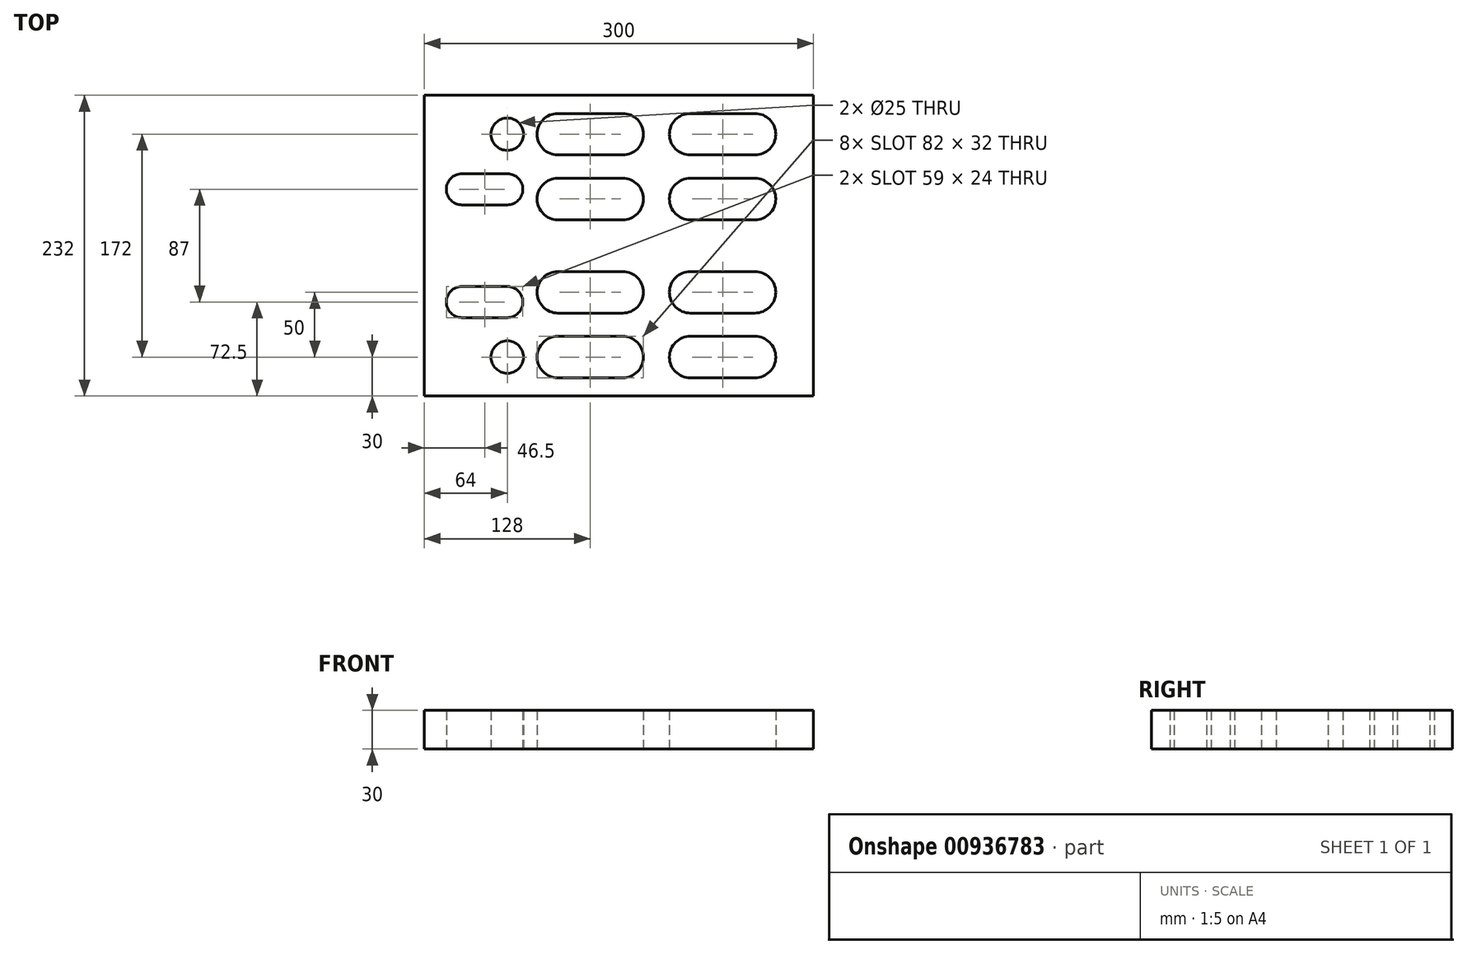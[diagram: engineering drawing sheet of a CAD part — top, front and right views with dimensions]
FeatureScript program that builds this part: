
annotation { "Feature Type Name" : "Feature", "Feature Type Description" : "" }
export const myFeature = defineFeature(function(context is Context, id is Id, definition is map)
    precondition{}
    {
        {
            var Q0;
            Q0=qCreatedBy(makeId("Top.planeOp"),FACE);
            var sketch = newSketch(context, id + "F0", { "sketchPlane" : qUnion([Q0])});
            skLineSegment(sketch, "E0.bottom", {"start": v(300, 116) * mm, "end": v(0, 116) * mm});
            skLineSegment(sketch, "E0.top", {"start": v(300, -116) * mm, "end": v(0, -116) * mm});
            skLineSegment(sketch, "E0.left", {"start": v(300, 116) * mm, "end": v(300, -116) * mm});
            skLineSegment(sketch, "E0.right", {"start": v(0, 116) * mm, "end": v(0, -116) * mm});
            skPoint(sketch, "E0.middle", {"position": v(0, 0) * mm});
            skArc(sketch, "E1", {"start": v(103, 102) * mm, "mid": v(87, 86) * mm, "end": v(103, 70) * mm});
            skArc(sketch, "E2", {"start": v(153, 70) * mm, "mid": v(169, 86) * mm, "end": v(153, 102) * mm});
            skLineSegment(sketch, "E3", {"start": v(103, 102) * mm, "end": v(153, 102) * mm});
            skLineSegment(sketch, "E4", {"start": v(103, 70) * mm, "end": v(153, 70) * mm});
            skLineSegment(sketch, "E5.1.0.0", {"start": v(205, 102) * mm, "end": v(255, 102) * mm});
            skArc(sketch, "E5.1.0.1", {"start": v(205, 102) * mm, "mid": v(189, 86) * mm, "end": v(205, 70) * mm});
            skLineSegment(sketch, "E5.1.0.2", {"start": v(205, 70) * mm, "end": v(255, 70) * mm});
            skArc(sketch, "E5.1.0.3", {"start": v(255, 70) * mm, "mid": v(271, 86) * mm, "end": v(255, 102) * mm});
            skLineSegment(sketch, "E5.direction1", {"start": v(103, 102) * mm, "end": v(205, 102) * mm, "construction": true});
            skArc(sketch, "E6.0.1.0", {"start": v(103, 52) * mm, "mid": v(87, 36) * mm, "end": v(103, 20) * mm});
            skLineSegment(sketch, "E6.0.1.1", {"start": v(103, 52) * mm, "end": v(153, 52) * mm});
            skArc(sketch, "E6.0.1.2", {"start": v(153, 20) * mm, "mid": v(169, 36) * mm, "end": v(153, 52) * mm});
            skLineSegment(sketch, "E6.0.1.3", {"start": v(103, 20) * mm, "end": v(153, 20) * mm});
            skArc(sketch, "E6.0.1.4", {"start": v(205, 52) * mm, "mid": v(189, 36) * mm, "end": v(205, 20) * mm});
            skLineSegment(sketch, "E6.0.1.5", {"start": v(205, 52) * mm, "end": v(255, 52) * mm});
            skArc(sketch, "E6.0.1.6", {"start": v(255, 20) * mm, "mid": v(271, 36) * mm, "end": v(255, 52) * mm});
            skLineSegment(sketch, "E6.0.1.7", {"start": v(205, 20) * mm, "end": v(255, 20) * mm});
            skLineSegment(sketch, "E6.direction1", {"start": v(103, 70) * mm, "end": v(128, 70) * mm, "construction": true});
            skLineSegment(sketch, "E6.direction2", {"start": v(103, 70) * mm, "end": v(103, 20) * mm, "construction": true});
            skCircle(sketch, "E7", {"center": v(64, 86) * mm, "radius": 12.5 * mm});
            skArc(sketch, "E8", {"start": v(29, 55.5) * mm, "mid": v(17, 43.5) * mm, "end": v(29, 31.5) * mm});
            skArc(sketch, "E9", {"start": v(64, 31.5) * mm, "mid": v(76, 43.5) * mm, "end": v(64, 55.5) * mm});
            skLineSegment(sketch, "E10", {"start": v(29, 55.5) * mm, "end": v(64, 55.5) * mm});
            skLineSegment(sketch, "E11", {"start": v(64, 31.5) * mm, "end": v(29, 31.5) * mm});
            skCircle(sketch, "E12.MirrorC", {"center": v(64, -86) * mm, "radius": 12.5 * mm});
            skLineSegment(sketch, "E13.MirrorCS", {"start": v(29, -55.5) * mm, "end": v(64, -55.5) * mm});
            skArc(sketch, "E14.MirrorCS", {"start": v(29, -55.5) * mm, "mid": v(17, -43.5) * mm, "end": v(29, -31.5) * mm});
            skLineSegment(sketch, "E15.MirrorCS", {"start": v(64, -31.5) * mm, "end": v(29, -31.5) * mm});
            skArc(sketch, "E16.MirrorCS", {"start": v(64, -31.5) * mm, "mid": v(76, -43.5) * mm, "end": v(64, -55.5) * mm});
            skArc(sketch, "E17.MirrorCS", {"start": v(103, -102) * mm, "mid": v(87, -86) * mm, "end": v(103, -70) * mm});
            skLineSegment(sketch, "E18.MirrorCS", {"start": v(103, -70) * mm, "end": v(153, -70) * mm});
            skArc(sketch, "E19.MirrorCS", {"start": v(153, -70) * mm, "mid": v(169, -86) * mm, "end": v(153, -102) * mm});
            skLineSegment(sketch, "E20.MirrorCS", {"start": v(103, -102) * mm, "end": v(153, -102) * mm});
            skLineSegment(sketch, "E21.MirrorCS", {"start": v(103, -52) * mm, "end": v(153, -52) * mm});
            skArc(sketch, "E22.MirrorCS", {"start": v(103, -52) * mm, "mid": v(87, -36) * mm, "end": v(103, -20) * mm});
            skLineSegment(sketch, "E23.MirrorCS", {"start": v(103, -20) * mm, "end": v(153, -20) * mm});
            skArc(sketch, "E24.MirrorCS", {"start": v(153, -20) * mm, "mid": v(169, -36) * mm, "end": v(153, -52) * mm});
            skArc(sketch, "E25.MirrorCS", {"start": v(205, -52) * mm, "mid": v(189, -36) * mm, "end": v(205, -20) * mm});
            skLineSegment(sketch, "E26.MirrorCS", {"start": v(205, -52) * mm, "end": v(255, -52) * mm});
            skArc(sketch, "E27.MirrorCS", {"start": v(255, -20) * mm, "mid": v(271, -36) * mm, "end": v(255, -52) * mm});
            skLineSegment(sketch, "E28.MirrorCS", {"start": v(205, -20) * mm, "end": v(255, -20) * mm});
            skArc(sketch, "E29.MirrorCS", {"start": v(205, -102) * mm, "mid": v(189, -86) * mm, "end": v(205, -70) * mm});
            skLineSegment(sketch, "E30.MirrorCS", {"start": v(205, -102) * mm, "end": v(255, -102) * mm});
            skArc(sketch, "E31.MirrorCS", {"start": v(255, -70) * mm, "mid": v(271, -86) * mm, "end": v(255, -102) * mm});
            skLineSegment(sketch, "E32.MirrorCS", {"start": v(205, -70) * mm, "end": v(255, -70) * mm});
            skArc(sketch, "E33.0", {"start": v(103, 101) * mm, "mid": v(88, 86) * mm, "end": v(103, 71) * mm});
            skLineSegment(sketch, "E33.1", {"start": v(103, 101) * mm, "end": v(153, 101) * mm});
            skArc(sketch, "E33.2", {"start": v(153, 71) * mm, "mid": v(168, 86) * mm, "end": v(153, 101) * mm});
            skLineSegment(sketch, "E33.3", {"start": v(103, 71) * mm, "end": v(153, 71) * mm});
            skArc(sketch, "E34.0", {"start": v(205, 101) * mm, "mid": v(190, 86) * mm, "end": v(205, 71) * mm});
            skLineSegment(sketch, "E34.1", {"start": v(205, 101) * mm, "end": v(255, 101) * mm});
            skArc(sketch, "E34.2", {"start": v(255, 71) * mm, "mid": v(270, 86) * mm, "end": v(255, 101) * mm});
            skLineSegment(sketch, "E34.3", {"start": v(205, 71) * mm, "end": v(255, 71) * mm});
            skArc(sketch, "E35.0", {"start": v(205, 51) * mm, "mid": v(190, 36) * mm, "end": v(205, 21) * mm});
            skLineSegment(sketch, "E35.1", {"start": v(205, 51) * mm, "end": v(255, 51) * mm});
            skArc(sketch, "E35.2", {"start": v(255, 21) * mm, "mid": v(270, 36) * mm, "end": v(255, 51) * mm});
            skLineSegment(sketch, "E35.3", {"start": v(205, 21) * mm, "end": v(255, 21) * mm});
            skArc(sketch, "E36.0", {"start": v(103, 51) * mm, "mid": v(88, 36) * mm, "end": v(103, 21) * mm});
            skLineSegment(sketch, "E36.1", {"start": v(103, 51) * mm, "end": v(153, 51) * mm});
            skArc(sketch, "E36.2", {"start": v(153, 21) * mm, "mid": v(168, 36) * mm, "end": v(153, 51) * mm});
            skLineSegment(sketch, "E36.3", {"start": v(103, 21) * mm, "end": v(153, 21) * mm});
            skArc(sketch, "E37.0", {"start": v(103, -51) * mm, "mid": v(88, -36) * mm, "end": v(103, -21) * mm});
            skLineSegment(sketch, "E37.1", {"start": v(103, -51) * mm, "end": v(153, -51) * mm});
            skArc(sketch, "E37.2", {"start": v(153, -21) * mm, "mid": v(168, -36) * mm, "end": v(153, -51) * mm});
            skLineSegment(sketch, "E37.3", {"start": v(103, -21) * mm, "end": v(153, -21) * mm});
            skArc(sketch, "E38.0", {"start": v(103, -101) * mm, "mid": v(88, -86) * mm, "end": v(103, -71) * mm});
            skLineSegment(sketch, "E38.1", {"start": v(103, -101) * mm, "end": v(153, -101) * mm});
            skArc(sketch, "E38.2", {"start": v(153, -71) * mm, "mid": v(168, -86) * mm, "end": v(153, -101) * mm});
            skLineSegment(sketch, "E38.3", {"start": v(103, -71) * mm, "end": v(153, -71) * mm});
            skArc(sketch, "E39.0", {"start": v(205, -51) * mm, "mid": v(190, -36) * mm, "end": v(205, -21) * mm});
            skLineSegment(sketch, "E39.1", {"start": v(205, -51) * mm, "end": v(255, -51) * mm});
            skArc(sketch, "E39.2", {"start": v(255, -21) * mm, "mid": v(270, -36) * mm, "end": v(255, -51) * mm});
            skLineSegment(sketch, "E39.3", {"start": v(205, -21) * mm, "end": v(255, -21) * mm});
            skArc(sketch, "E40.0", {"start": v(205, -101) * mm, "mid": v(190, -86) * mm, "end": v(205, -71) * mm});
            skLineSegment(sketch, "E40.1", {"start": v(205, -101) * mm, "end": v(255, -101) * mm});
            skArc(sketch, "E40.2", {"start": v(255, -71) * mm, "mid": v(270, -86) * mm, "end": v(255, -101) * mm});
            skLineSegment(sketch, "E40.3", {"start": v(205, -71) * mm, "end": v(255, -71) * mm});
            skLineSegment(sketch, "E41.0", {"start": v(29, 54.5) * mm, "end": v(64, 54.5) * mm});
            skArc(sketch, "E41.1", {"start": v(29, 54.5) * mm, "mid": v(18, 43.5) * mm, "end": v(29, 32.5) * mm});
            skLineSegment(sketch, "E41.2", {"start": v(64, 32.5) * mm, "end": v(29, 32.5) * mm});
            skArc(sketch, "E41.3", {"start": v(64, 32.5) * mm, "mid": v(75, 43.5) * mm, "end": v(64, 54.5) * mm});
            skArc(sketch, "E42.0", {"start": v(29, -54.5) * mm, "mid": v(18, -43.5) * mm, "end": v(29, -32.5) * mm});
            skLineSegment(sketch, "E42.1", {"start": v(29, -54.5) * mm, "end": v(64, -54.5) * mm});
            skArc(sketch, "E42.2", {"start": v(64, -32.5) * mm, "mid": v(75, -43.5) * mm, "end": v(64, -54.5) * mm});
            skLineSegment(sketch, "E42.3", {"start": v(64, -32.5) * mm, "end": v(29, -32.5) * mm});
            skCircle(sketch, "E43", {"center": v(103, 86) * mm, "radius": 11 * mm, "construction": true});
            skCircle(sketch, "E44", {"center": v(153, 86) * mm, "radius": 11 * mm, "construction": true});
            skLineSegment(sketch, "E45", {"start": v(103, 86) * mm, "end": v(153, 86) * mm, "construction": true});
            skPoint(sketch, "E46", {"position": v(128, 86) * mm});
            skCircle(sketch, "E47", {"center": v(128, 86) * mm, "radius": 11 * mm, "construction": true});
            skCircle(sketch, "E48", {"center": v(29, 43.5) * mm, "radius": 11 * mm, "construction": true});
            skCircle(sketch, "E49", {"center": v(64, 43.5) * mm, "radius": 11 * mm, "construction": true});
            skLineSegment(sketch, "E50", {"start": v(29, 43.5) * mm, "end": v(64, 43.5) * mm, "construction": true});
            skCircle(sketch, "E51", {"center": v(46.5, 43.5) * mm, "radius": 11 * mm, "construction": true});
            skLineSegment(sketch, "E52", {"start": v(205, 86) * mm, "end": v(255, 86) * mm, "construction": true});
            skPoint(sketch, "E53", {"position": v(230, 86) * mm});
            skSolve(sketch);
        }
        {
            var Q0;
            Q0 = qSketchRegion(id + "F0", true);
            extrude(context, id + "F1", {"entities" : qUnion([Q0]), "depth" : 30 * mm, "offsetDistance" : 25 * mm});
        }
    });
